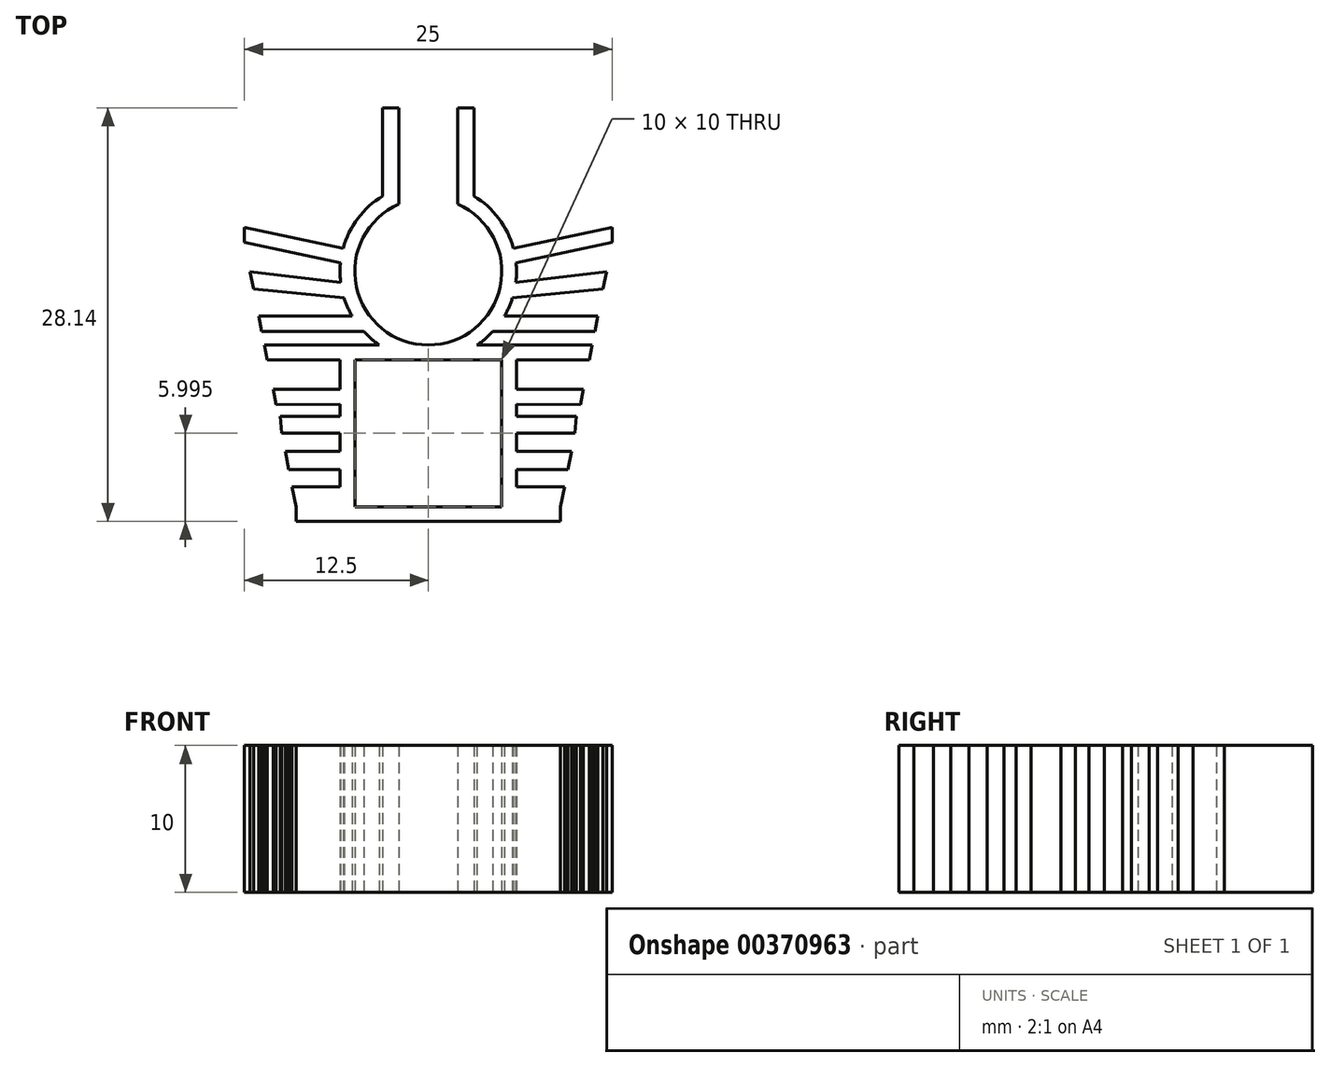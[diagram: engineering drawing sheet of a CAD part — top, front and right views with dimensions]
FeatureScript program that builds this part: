
annotation { "Feature Type Name" : "Feature", "Feature Type Description" : "" }
export const myFeature = defineFeature(function(context is Context, id is Id, definition is map)
    precondition{}
    {
        {
            var Q0;
            Q0=qCreatedBy(makeId("Top.planeOp"),FACE);
            var sketch = newSketch(context, id + "F0", { "sketchPlane" : qUnion([Q0])});
            skArc(sketch, "E0", {"start": v(0, -5) * mm, "mid": v(4.9, -1.02) * mm, "end": v(2, 4.58) * mm});
            skArc(sketch, "E1", {"start": v(3.32, -5) * mm, "mid": v(6, 0.13) * mm, "end": v(3.1, 5.14) * mm});
            skLineSegment(sketch, "E2.top", {"start": v(0, -17) * mm, "end": v(6, -17) * mm});
            skLineSegment(sketch, "E2.right", {"start": v(6, -6) * mm, "end": v(6, -8.01) * mm});
            skLineSegment(sketch, "E3.bottom", {"start": v(5, -6) * mm, "end": v(0, -6) * mm});
            skLineSegment(sketch, "E3.top", {"start": v(5, -16) * mm, "end": v(0, -16) * mm});
            skLineSegment(sketch, "E3.left", {"start": v(5, -6) * mm, "end": v(5, -16) * mm});
            skLineSegment(sketch, "E4.trimOffspring", {"start": v(3.32, -5) * mm, "end": v(6, -5) * mm});
            skLineSegment(sketch, "E5.right", {"start": v(9, -17) * mm, "end": v(9, -16) * mm});
            skLineSegment(sketch, "E6", {"start": v(0, 14.57) * mm, "end": v(0, -27.43) * mm});
            skPoint(sketch, "E7.end.orphan", {"position": v(-12.65, 3) * mm});
            skPoint(sketch, "E5.left.end.orphan", {"position": v(-9, 3) * mm});
            skLineSegment(sketch, "E8.trimOffspring", {"start": v(0, -17) * mm, "end": v(9, -17) * mm});
            skPoint(sketch, "E5.bottom.end.orphan", {"position": v(-6, -17) * mm});
            skPoint(sketch, "E5.bottom.start.orphan", {"position": v(-9, -17) * mm});
            skLineSegment(sketch, "E9", {"start": v(12.5, 3) * mm, "end": v(12.5, 1.97) * mm});
            skLineSegment(sketch, "E10", {"start": v(12.5, 1.97) * mm, "end": v(5.97, 0.58) * mm});
            skLineSegment(sketch, "E11", {"start": v(12.5, 3) * mm, "end": v(5.8, 1.57) * mm});
            skLineSegment(sketch, "E12", {"start": v(12.12, 0) * mm, "end": v(11.88, -1.2) * mm});
            skLineSegment(sketch, "E13", {"start": v(4.39, -4.1) * mm, "end": v(11.32, -4.1) * mm});
            skLineSegment(sketch, "E14", {"start": v(5.17, -3.04) * mm, "end": v(11.52, -3.04) * mm});
            skLineSegment(sketch, "E15", {"start": v(6, -5) * mm, "end": v(11.14, -5) * mm});
            skLineSegment(sketch, "E16", {"start": v(6, -6) * mm, "end": v(10.95, -6) * mm});
            skLineSegment(sketch, "E17", {"start": v(6, -8.01) * mm, "end": v(10.55, -8.01) * mm});
            skLineSegment(sketch, "E18", {"start": v(6, -9.04) * mm, "end": v(10.35, -9.05) * mm});
            skLineSegment(sketch, "E19", {"start": v(6, -11) * mm, "end": v(9.97, -11) * mm});
            skLineSegment(sketch, "E20", {"start": v(6, -12.24) * mm, "end": v(9.73, -12.24) * mm});
            skLineSegment(sketch, "E21", {"start": v(6, -13.47) * mm, "end": v(9.5, -13.47) * mm});
            skLineSegment(sketch, "E22", {"start": v(6, -14.66) * mm, "end": v(9.26, -14.66) * mm});
            skLineSegment(sketch, "E23", {"start": v(5.72, -1.8) * mm, "end": v(11.88, -1.2) * mm});
            skLineSegment(sketch, "E24", {"start": v(5.95, -0.74) * mm, "end": v(12.12, 0) * mm});
            skPoint(sketch, "E24.endSnap0", {"position": v(5, 0) * mm});
            skLineSegment(sketch, "E25", {"start": v(2, 11.14) * mm, "end": v(2, 4.58) * mm});
            skLineSegment(sketch, "E26", {"start": v(2, 11.14) * mm, "end": v(3.1, 11.14) * mm});
            skLineSegment(sketch, "E27", {"start": v(3.1, 11.14) * mm, "end": v(3.1, 5.14) * mm});
            skLineSegment(sketch, "E28.trimOffspring", {"start": v(11.52, -3.04) * mm, "end": v(11.32, -4.1) * mm});
            skLineSegment(sketch, "E29.trimOffspring", {"start": v(11.14, -5) * mm, "end": v(10.95, -6) * mm});
            skLineSegment(sketch, "E30.trimOffspring", {"start": v(9.26, -14.66) * mm, "end": v(9, -16) * mm});
            skLineSegment(sketch, "E31", {"start": v(9.5, -13.47) * mm, "end": v(9.73, -12.24) * mm});
            skLineSegment(sketch, "E32", {"start": v(6, -9.86) * mm, "end": v(10.05, -9.87) * mm});
            skLineSegment(sketch, "E33", {"start": v(9.97, -11) * mm, "end": v(10.05, -9.87) * mm});
            skLineSegment(sketch, "E34", {"start": v(10.35, -9.05) * mm, "end": v(10.55, -8.01) * mm});
            skLineSegment(sketch, "E35.trimOffspring", {"start": v(6, -9.04) * mm, "end": v(6, -9.86) * mm});
            skLineSegment(sketch, "E36.trimOffspring", {"start": v(6, -11) * mm, "end": v(6, -12.24) * mm});
            skLineSegment(sketch, "E37.trimOffspring", {"start": v(6, -13.47) * mm, "end": v(6, -14.66) * mm});
            skLineSegment(sketch, "E38.trimOffspring", {"start": v(6, -17) * mm, "end": v(6, -17) * mm});
            skPoint(sketch, "E39.orphan", {"position": v(6, -16) * mm});
            skLineSegment(sketch, "E40.MirrorCS", {"start": v(-6, -17) * mm, "end": v(-6, -17) * mm});
            skLineSegment(sketch, "E41.MirrorCS", {"start": v(-6, -9.04) * mm, "end": v(-6, -9.86) * mm});
            skLineSegment(sketch, "E42.MirrorCS", {"start": v(-12.12, 0) * mm, "end": v(-11.88, -1.2) * mm});
            skLineSegment(sketch, "E43.MirrorCS", {"start": v(-2, 11.14) * mm, "end": v(-3.1, 11.14) * mm});
            skLineSegment(sketch, "E44.MirrorCS", {"start": v(-9.5, -13.47) * mm, "end": v(-9.73, -12.24) * mm});
            skLineSegment(sketch, "E45.MirrorCS", {"start": v(-6, -11) * mm, "end": v(-6, -12.24) * mm});
            skLineSegment(sketch, "E46.MirrorCS", {"start": v(-10.35, -9.05) * mm, "end": v(-10.55, -8.01) * mm});
            skLineSegment(sketch, "E47.MirrorCS", {"start": v(-11.52, -3.04) * mm, "end": v(-11.32, -4.1) * mm});
            skLineSegment(sketch, "E48.MirrorCS", {"start": v(-9, -17) * mm, "end": v(-9, -16) * mm});
            skLineSegment(sketch, "E49.MirrorCS", {"start": v(-12.5, 3) * mm, "end": v(-12.5, 1.97) * mm});
            skLineSegment(sketch, "E50.MirrorCS", {"start": v(-11.14, -5) * mm, "end": v(-10.95, -6) * mm});
            skLineSegment(sketch, "E51.MirrorCS", {"start": v(-6, -13.47) * mm, "end": v(-6, -14.66) * mm});
            skLineSegment(sketch, "E52.MirrorCS", {"start": v(-9.97, -11) * mm, "end": v(-10.05, -9.87) * mm});
            skLineSegment(sketch, "E53.MirrorCS", {"start": v(-9.26, -14.66) * mm, "end": v(-9, -16) * mm});
            skLineSegment(sketch, "E54.MirrorCS", {"start": v(0, -17) * mm, "end": v(-6, -17) * mm});
            skLineSegment(sketch, "E55.MirrorCS", {"start": v(-4.39, -4.1) * mm, "end": v(-11.32, -4.1) * mm});
            skArc(sketch, "E56.MirrorCS", {"start": v(0, -5) * mm, "mid": v(-4.9, -1.02) * mm, "end": v(-2, 4.58) * mm});
            skLineSegment(sketch, "E57.MirrorCS", {"start": v(-6, -14.66) * mm, "end": v(-9.26, -14.66) * mm});
            skArc(sketch, "E58.MirrorCS", {"start": v(-3.32, -5) * mm, "mid": v(-6, 0.13) * mm, "end": v(-3.1, 5.14) * mm});
            skLineSegment(sketch, "E59.MirrorCS", {"start": v(-6, -6) * mm, "end": v(-10.95, -6) * mm});
            skLineSegment(sketch, "E60.MirrorCS", {"start": v(-6, -11) * mm, "end": v(-9.97, -11) * mm});
            skLineSegment(sketch, "E61.MirrorCS", {"start": v(-6, -5) * mm, "end": v(-11.14, -5) * mm});
            skLineSegment(sketch, "E62.MirrorCS", {"start": v(-6, -6) * mm, "end": v(-6, -8.01) * mm});
            skLineSegment(sketch, "E63.MirrorCS", {"start": v(-3.1, 11.14) * mm, "end": v(-3.1, 5.14) * mm});
            skLineSegment(sketch, "E64.MirrorCS", {"start": v(-5, -16) * mm, "end": v(0, -16) * mm});
            skLineSegment(sketch, "E65.MirrorCS", {"start": v(-5.17, -3.04) * mm, "end": v(-11.52, -3.04) * mm});
            skPoint(sketch, "E66.MirrorP", {"position": v(-5, 0) * mm});
            skLineSegment(sketch, "E67.MirrorCS", {"start": v(-5, -6) * mm, "end": v(-5, -16) * mm});
            skLineSegment(sketch, "E68.MirrorCS", {"start": v(-5.72, -1.8) * mm, "end": v(-11.88, -1.2) * mm});
            skLineSegment(sketch, "E69.MirrorCS", {"start": v(-5, -6) * mm, "end": v(0, -6) * mm});
            skLineSegment(sketch, "E70.MirrorCS", {"start": v(-3.32, -5) * mm, "end": v(-6, -5) * mm});
            skLineSegment(sketch, "E71.MirrorCS", {"start": v(0, -17) * mm, "end": v(-9, -17) * mm});
            skPoint(sketch, "E72.MirrorP", {"position": v(-6, -16) * mm});
            skLineSegment(sketch, "E73.MirrorCS", {"start": v(-12.5, 1.97) * mm, "end": v(-5.97, 0.58) * mm});
            skLineSegment(sketch, "E74.MirrorCS", {"start": v(-12.5, 3) * mm, "end": v(-5.8, 1.57) * mm});
            skLineSegment(sketch, "E75.MirrorCS", {"start": v(-2, 11.14) * mm, "end": v(-2, 4.58) * mm});
            skLineSegment(sketch, "E76.MirrorCS", {"start": v(-6, -13.47) * mm, "end": v(-9.5, -13.47) * mm});
            skLineSegment(sketch, "E77.MirrorCS", {"start": v(-6, -9.86) * mm, "end": v(-10.05, -9.87) * mm});
            skLineSegment(sketch, "E78.MirrorCS", {"start": v(-6, -12.24) * mm, "end": v(-9.73, -12.24) * mm});
            skLineSegment(sketch, "E79.MirrorCS", {"start": v(-5.95, -0.74) * mm, "end": v(-12.12, 0) * mm});
            skLineSegment(sketch, "E80.MirrorCS", {"start": v(-6, -8.01) * mm, "end": v(-10.55, -8.01) * mm});
            skLineSegment(sketch, "E81.MirrorCS", {"start": v(-6, -9.04) * mm, "end": v(-10.35, -9.05) * mm});
            skSolve(sketch);
        }
        {
            var Q0;
            {var subQ6=sQuery(id+"F0.wireOp",EDGE,"E0");Q0=makeQuery(id+"F0.imprint","IMPRINT",FACE,{"disambiguationData":[TD([[makeQuery(id+"F0.imprint","IMPRINT",EDGE,{"derivedFrom":subQ6}),-1.0]])]});}
            var Q1;
            Q1=makeQuery(id+"F0.imprint","IMPRINT",FACE,{"disambiguationData":[TD([[makeQuery(id+"F0.imprint","IMPRINT",EDGE,{"derivedFrom":sQuery(id+"F0.wireOp",EDGE,"E9")}),-1.0]])]});
            var Q2;
            Q2=makeQuery(id+"F0.imprint","IMPRINT",FACE,{"disambiguationData":[TD([[makeQuery(id+"F0.imprint","IMPRINT",EDGE,{"derivedFrom":sQuery(id+"F0.wireOp",EDGE,"E12")}),-1.0]])]});
            var Q3;
            {var subQ0=sQuery(id+"F0.wireOp",EDGE,"E13");Q3=makeQuery(id+"F0.imprint","IMPRINT",FACE,{"disambiguationData":[TD([[makeQuery(id+"F0.imprint","IMPRINT",EDGE,{"derivedFrom":subQ0}),1.0]])]});}
            var Q4;
            Q4=makeQuery(id+"F0.imprint","IMPRINT",FACE,{"disambiguationData":[TD([[makeQuery(id+"F0.imprint","IMPRINT",EDGE,{"derivedFrom":sQuery(id+"F0.wireOp",EDGE,"E41.MirrorCS")}),1.0]])]});
            var Q5;
            Q5=makeQuery(id+"F0.imprint","IMPRINT",FACE,{"disambiguationData":[TD([[makeQuery(id+"F0.imprint","IMPRINT",EDGE,{"derivedFrom":sQuery(id+"F0.wireOp",EDGE,"E49.MirrorCS")}),1.0]])]});
            var Q6;
            Q6=makeQuery(id+"F0.imprint","IMPRINT",FACE,{"disambiguationData":[TD([[makeQuery(id+"F0.imprint","IMPRINT",EDGE,{"derivedFrom":sQuery(id+"F0.wireOp",EDGE,"E42.MirrorCS")}),1.0]])]});
            var Q7;
            Q7=makeQuery(id+"F0.imprint","IMPRINT",FACE,{"disambiguationData":[TD([[makeQuery(id+"F0.imprint","IMPRINT",EDGE,{"derivedFrom":sQuery(id+"F0.wireOp",EDGE,"E47.MirrorCS")}),1.0]])]});
            extrude(context, id + "F1", {"entities" : qUnion([Q0, Q1, Q2, Q3, Q4, Q5, Q6, Q7]), "depth" : 10 * mm});
        }
    });
